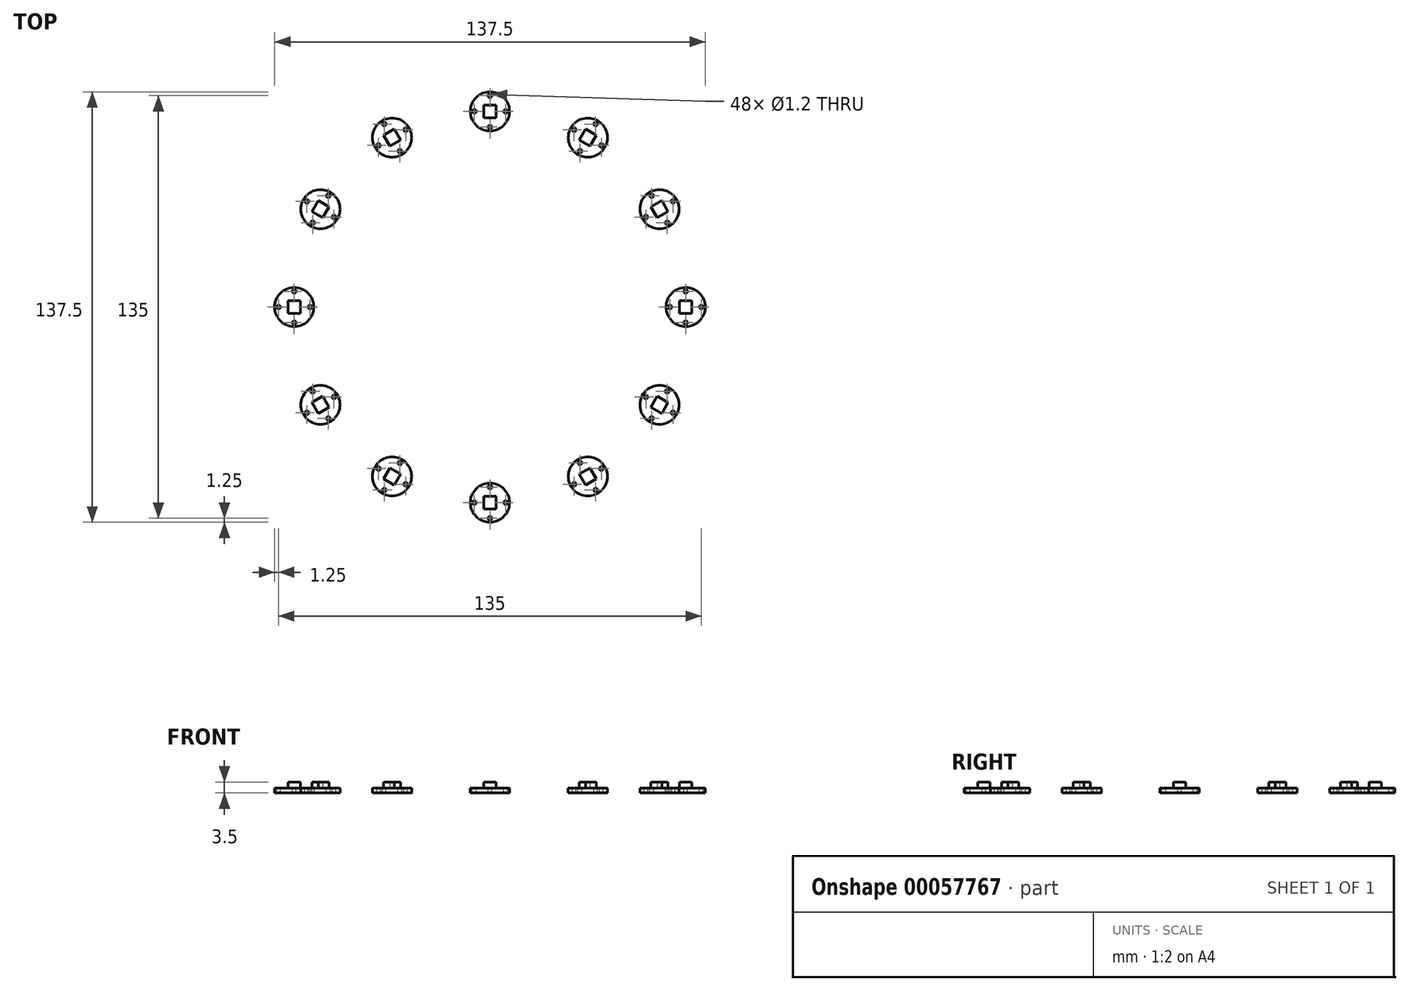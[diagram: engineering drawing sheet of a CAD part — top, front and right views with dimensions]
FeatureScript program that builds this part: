
annotation { "Feature Type Name" : "Feature", "Feature Type Description" : "" }
export const myFeature = defineFeature(function(context is Context, id is Id, definition is map)
    precondition{}
    {
        {
            var Q0;
            Q0=qCreatedBy(makeId("Top.planeOp"),FACE);
            var sketch = newSketch(context, id + "F0", { "sketchPlane" : qUnion([Q0])});
            skCircle(sketch, "E0", {"center": v(0, 0) * mm, "radius": 6.25 * mm});
            skSolve(sketch);
        }
        {
            var Q0;
            Q0 = qSketchRegion(id + "F0", true);
            extrude(context, id + "F1", {"entities" : qUnion([Q0]), "depth" : 1.6 * mm});
        }
        {
            var Q0;
            Q0=makeQuery(id+"F1.opExtrude","CAP_FACE",FACE,{"disambiguationData":[OSD([sQuery(id+"F0.wireOp",EDGE,"E0")])],"isStart":false});
            var sketch = newSketch(context, id + "F2", { "sketchPlane" : qUnion([Q0])});
            skCircle(sketch, "E1.cCircle", {"center": v(0, 0) * mm, "radius": 2 * mm, "construction": true});
            skLineSegment(sketch, "E1.0", {"start": v(-2, -2) * mm, "end": v(-2, 2) * mm});
            skLineSegment(sketch, "E1.1", {"start": v(-2, 2) * mm, "end": v(2, 2) * mm});
            skLineSegment(sketch, "E1.2", {"start": v(2, 2) * mm, "end": v(2, -2) * mm});
            skLineSegment(sketch, "E1.3", {"start": v(2, -2) * mm, "end": v(-2, -2) * mm});
            skPoint(sketch, "E1.0.midPoint", {"position": v(-2, 0) * mm});
            skSolve(sketch);
        }
        {
            var Q0;
            Q0 = qSketchRegion(id + "F2", true);
            extrude(context, id + "F3", {"entities" : qUnion([Q0]), "operationType" : NewBodyOperationType.ADD, "depth" : 1.9 * mm});
        }
        {
            var Q0;
            Q0=makeQuery(id+"F1.opExtrude","CAP_FACE",FACE,{"disambiguationData":[OSD([sQuery(id+"F0.wireOp",EDGE,"E0")])],"isStart":false});
            var sketch = newSketch(context, id + "F4", { "sketchPlane" : qUnion([Q0])});
            skCircle(sketch, "E2", {"center": v(0, 0) * mm, "radius": 5 * mm, "construction": true});
            skLineSegment(sketch, "E3", {"start": v(0, 0) * mm, "end": v(0, 7.96) * mm, "construction": true});
            skPoint(sketch, "E3.endSnap0", {"position": v(0, 2) * mm});
            skCircle(sketch, "E4", {"center": v(0, 5) * mm, "radius": 0.6 * mm});
            skCircle(sketch, "E5.1.0", {"center": v(-5, 0) * mm, "radius": 0.6 * mm});
            skCircle(sketch, "E5.2.0", {"center": v(0, -5) * mm, "radius": 0.6 * mm});
            skCircle(sketch, "E5.3.0", {"center": v(5, 0) * mm, "radius": 0.6 * mm});
            skSolve(sketch);
        }
        {
            var Q0;
            Q0 = qSketchRegion(id + "F4", true);
            extrude(context, id + "F5", {"entities" : qUnion([Q0]), "operationType" : NewBodyOperationType.REMOVE, "oppositeDirection" : true, "depth" : 25 * mm});
        }
        {
            var Q0;
            Q0=qCreatedBy(makeId("Top.planeOp"),FACE);
            var sketch = newSketch(context, id + "F6", { "sketchPlane" : qUnion([Q0])});
            skCircle(sketch, "E6", {"center": v(0, 62.5) * mm, "radius": 62.5 * mm});
            skSolve(sketch);
        }
        {
            var Q0;
            Q0=makeQuery(id+"F1.opExtrude","SWEPT_BODY",BODY,{"disambiguationData":[OSD([sQuery(id+"F0.wireOp",EDGE,"E0")])]});
            var Q1;
            Q1=sQuery(id+"F6.wireOp",EDGE,"E6");
            circularPattern(context, id + "F7", {"entities" : qUnion([Q0]), "axis" : qUnion([Q1]), "angle" : 30 * degree, "instanceCount" : 12});
        }
    });
